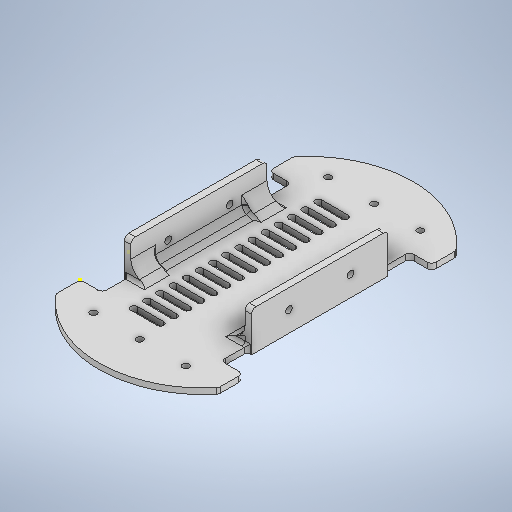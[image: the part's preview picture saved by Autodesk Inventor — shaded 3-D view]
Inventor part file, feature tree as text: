
AUTODESK INVENTOR PART (.ipt)
format: ipt  version: 2025.2 (Build 292293000, 293)  size: 808,448 bytes
history: native  units: mm
features: fillet x34, sketch x15, extrude x12
ambient origin geometry x8: Origin, YZ Plane, XZ Plane, XY Plane, X Axis, Y Axis, Z Axis, Center Point
bodies: Solid1 (feature_tree)
feature tree (61):
  extrude  "Extrusion1"  Depth=11.0mm
  fillet  "Face Fillet1"
  fillet  "Face Fillet2"
  fillet  "Face Fillet3"
  fillet  "Face Fillet4"
  fillet  "Face Fillet5"
  fillet  "Face Fillet6"
  fillet  "Face Fillet7"
  fillet  "Face Fillet8"
  fillet  "Face Fillet9"
  fillet  "Face Fillet10"
  fillet  "Face Fillet11"
  fillet  "Face Fillet12"
  sketch  "Sketch5"  dims[d3=11.0mm d4=17.5mm]
  sketch  "Sketch6"  dims[d5=17.5mm d11=74.0mm]
  sketch  "Sketch7"  dims[d12=74.0mm d15=27.0mm]
  sketch  "Sketch8"  dims[d16=27.0mm d17=2.6mm d18=0.0mm]
  sketch  "Sketch9"  dims[d19=2.0mm d20=2.0mm]
  extrude  "Extrusion5"  Depth=17.5mm
  extrude  "Extrusion6"  Depth=74.0mm
  extrude  "Extrusion7"  Depth=74.0mm
  extrude  "Extrusion8"  Depth=2.6mm TaperAngle=0.0deg
  sketch  "Sketch13"  dims[d25=2.0mm d26=2.0mm]
  sketch  "Sketch14"  dims[d27=2.0mm d48=2.0mm]
  extrude  "Extrusion9"  Depth=2.0mm
  extrude  "Extrusion10"  Depth=2.0mm
  fillet  "Face Fillet13"
  fillet  "Face Fillet14"
  fillet  "Face Fillet15"
  fillet  "Face Fillet16"
  extrude  "Extrusion12"  Depth=2.0mm
  extrude  "Extrusion14"  Depth=2.0mm
  sketch  "Sketch16"  dims[d63=1.5mm d65=21.0mm d66=21.0mm d67=10.9mm d68=2.9mm d69=2.9mm d70=2.9mm d71=10.0mm d72=3.0mm d73=3.0mm d74=3.0mm d87=18.0mm d88=82.0mm d89=31.0mm]
  extrude  "Extrusion15"  Depth=2.0mm
  extrude  "Extrusion16"  Depth=2.0mm
  sketch  "Sketch18"  dims[d91=31.0mm]
  extrude  "Extrusion17"  Depth=3.0mm
  fillet  "Fillet1"  Radius=21.0mm
  fillet  "Fillet2"  Radius=10.9mm
  fillet  "Fillet3"  Radius=2.9mm
  fillet  "Fillet4"  Radius=2.9mm
  fillet  "Face Fillet19"
  fillet  "Face Fillet20"
  fillet  "Face Fillet21"
  fillet  "Face Fillet22"
  fillet  "Face Fillet23"
  fillet  "Face Fillet24"
  fillet  "Fillet5"  Radius=2.9mm
  fillet  "Fillet6"  Radius=10.0mm
  fillet  "Fillet7"  Radius=3.0mm
  fillet  "Fillet8"  Radius=3.0mm
  fillet  "Fillet9"  Radius=3.0mm
  fillet  "Fillet10"  Radius=18.0mm
  fillet  "Fillet11"  Radius=82.0mm
  fillet  "Fillet12"  Radius=31.0mm
  sketch  "Sketch1"  dims[d1=86.0mm d2=11.0mm]
  sketch  "Sketch10"  dims[d21=2.0mm d22=2.0mm]
  sketch  "Sketch11"  dims[d23=2.0mm d24=2.0mm]
  sketch  "Sketch15"  dims[d49=2.0mm d50=2.0mm]
  sketch  "Sketch17"  dims[d90=31.0mm]
  sketch  "Sketch19"  dims[d92=18.0mm d93=2.0mm d94=0.0mm d95=2.0mm d96=0.0mm d97=1.0mm d98=0.0mm d99=1.0mm d100=0.0mm d101=14.0mm d102=14.0mm d103=18.0mm d104=9.3mm d105=9.3mm d106=3.0mm d107=3.0mm d108=3.0mm d109=3.0mm d110=40.0mm d111=0.0mm d112=40.0mm d113=0.0mm d114=2.0mm d115=2.0mm d116=2.0mm d117=2.0mm d120=10.0mm d121=0.0mm d125=86.0mm d126=0.5mm d127=0.5mm d128=12.0mm d129=15.0mm d130=3.0mm d131=3.0mm d132=3.0mm d133=3.0mm d134=3.0mm d135=3.0mm d136=3.0mm d137=3.0mm d138=3.0mm d139=3.0mm d140=3.0mm d141=3.0mm d142=3.0mm d143=3.0mm d144=3.0mm d145=3.0mm d146=3.0mm d147=3.0mm d148=3.0mm d149=3.0mm d150=3.0mm d151=3.0mm d152=3.0mm d153=3.0mm d154=3.0mm d155=3.0mm d156=3.0mm d157=3.0mm d158=3.0mm d159=40.0mm d160=0.0mm d163=1.5mm d164=1.5mm d165=13.5mm d166=13.5mm d167=1.5mm d168=1.5mm d169=9.0mm d170=4.0mm d171=9.0mm d172=4.0mm d173=1.5mm d174=4.0mm d175=1.5mm d176=9.0mm d177=9.0mm d178=10.0mm d179=0.0mm d180=10.0mm d181=0.0mm d182=5.0mm d183=5.0mm d184=45.0mm d185=0.0mm d186=6.67mm d187=6.67mm d188=6.67mm d189=6.67mm d190=3.0mm d191=3.0mm d192=1.4mm d193=1.4mm d194=1.4mm d195=1.4mm d196=1.4mm d197=1.4mm d198=1.4mm d199=1.4mm d200=1.4mm d201=1.4mm d202=1.4mm d203=1.4mm d122=0.5mm d123=0.872665mm]
